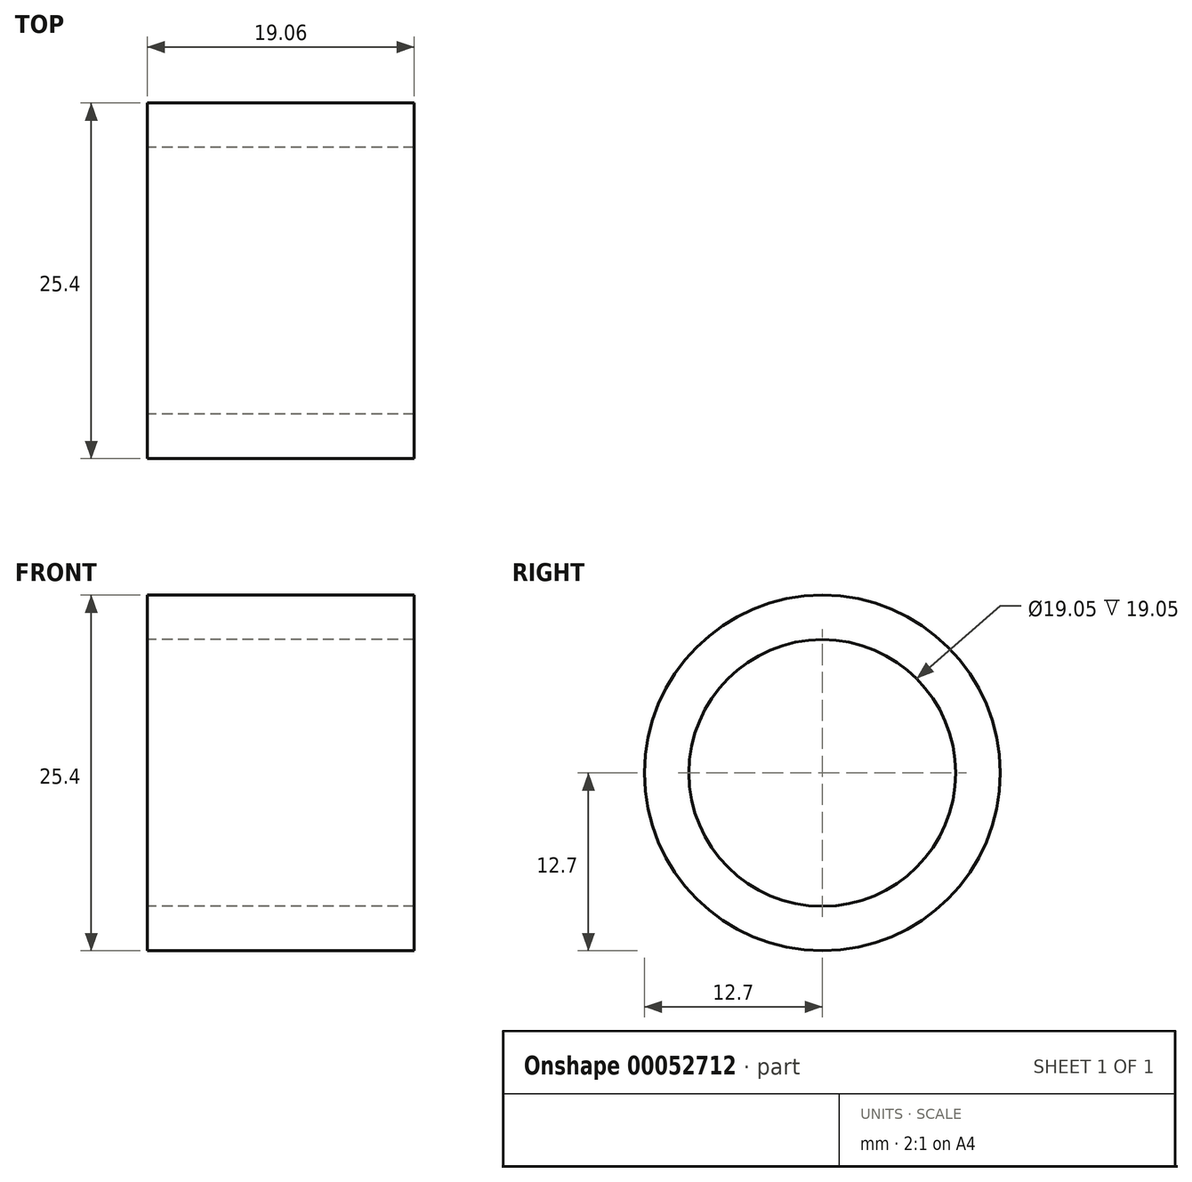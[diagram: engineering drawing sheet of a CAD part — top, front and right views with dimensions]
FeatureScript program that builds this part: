
annotation { "Feature Type Name" : "Feature", "Feature Type Description" : "" }
export const myFeature = defineFeature(function(context is Context, id is Id, definition is map)
    precondition{}
    {
        {
            var Q0;
            Q0=qCreatedBy(makeId("Right.planeOp"),FACE);
            var sketch = newSketch(context, id + "F0", { "sketchPlane" : qUnion([Q0])});
            skCircle(sketch, "E0", {"center": v(0, 0) * mm, "radius": 9.53 * mm});
            skCircle(sketch, "E1", {"center": v(0, 0) * mm, "radius": 12.7 * mm});
            skSolve(sketch);
        }
        {
            var Q0;
            Q0=makeQuery(id+"F0.imprint","IMPRINT",FACE,{"disambiguationData":[TD([[makeQuery(id+"F0.imprint","IMPRINT",EDGE,{"derivedFrom":sQuery(id+"F0.wireOp",EDGE,"E0")}),-1.0]])]});
            extrude(context, id + "F1", {"entities" : qUnion([Q0]), "depth" : 19.05 * mm, "symmetric" : true});
        }
    });
